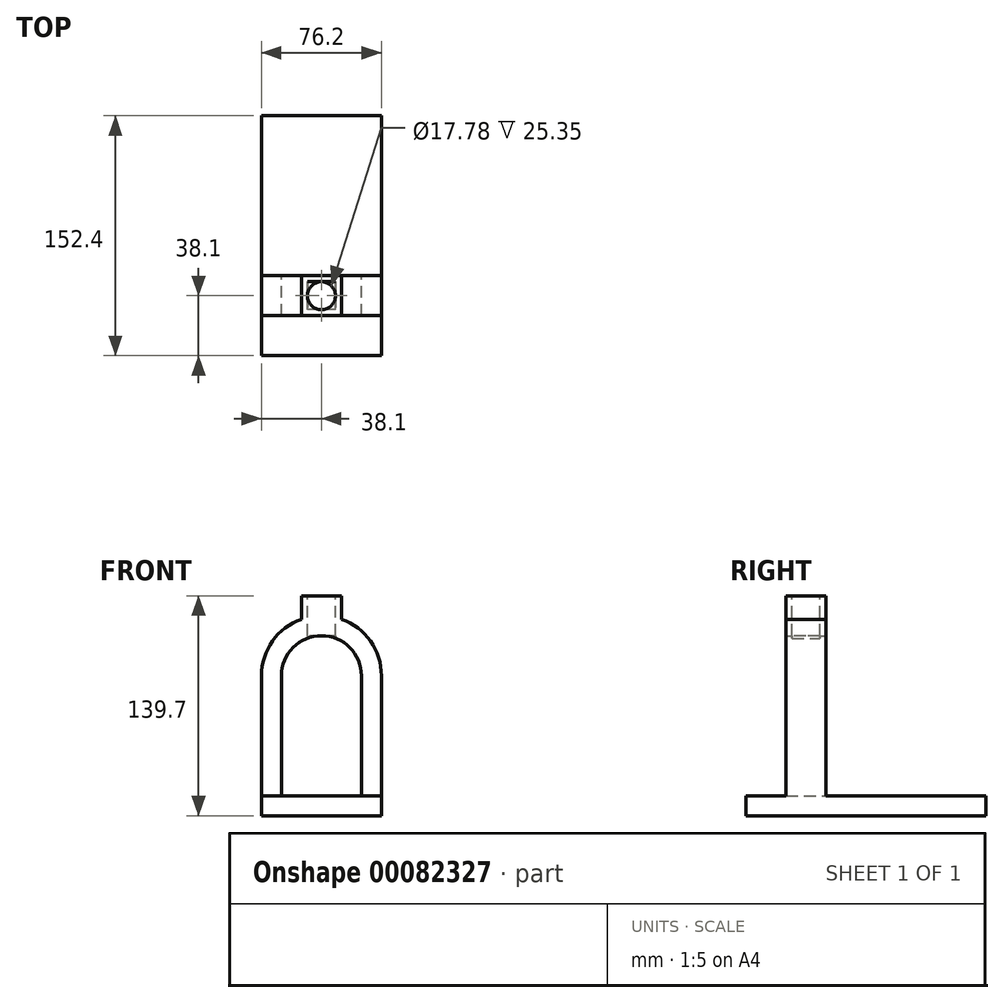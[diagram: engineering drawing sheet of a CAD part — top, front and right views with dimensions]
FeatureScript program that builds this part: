
annotation { "Feature Type Name" : "Feature", "Feature Type Description" : "" }
export const myFeature = defineFeature(function(context is Context, id is Id, definition is map)
    precondition{}
    {
        {
            var Q0;
            Q0=qCreatedBy(makeId("Front.planeOp"),FACE);
            var sketch = newSketch(context, id + "F0", { "sketchPlane" : qUnion([Q0])});
            skArc(sketch, "E0", {"start": v(25.4, 72.85) * mm, "mid": v(0, 98.25) * mm, "end": v(-25.4, 72.85) * mm});
            skArc(sketch, "E1", {"start": v(38.1, 72.85) * mm, "mid": v(31.1, 94.84) * mm, "end": v(12.7, 108.77) * mm});
            skLineSegment(sketch, "E2", {"start": v(38.1, 72.85) * mm, "end": v(38.1, -3.35) * mm});
            skLineSegment(sketch, "E3", {"start": v(-38.1, 72.85) * mm, "end": v(-38.1, -3.35) * mm});
            skLineSegment(sketch, "E4", {"start": v(-25.4, 72.85) * mm, "end": v(-25.4, -3.35) * mm});
            skLineSegment(sketch, "E5", {"start": v(25.4, 72.85) * mm, "end": v(25.4, -3.35) * mm});
            skLineSegment(sketch, "E6", {"start": v(38.1, -3.35) * mm, "end": v(25.4, -3.35) * mm});
            skLineSegment(sketch, "E7.trimOffspring", {"start": v(-25.4, -3.35) * mm, "end": v(-38.1, -3.35) * mm});
            skLineSegment(sketch, "E8", {"start": v(0, 123.65) * mm, "end": v(12.7, 123.65) * mm});
            skLineSegment(sketch, "E9", {"start": v(0, 123.65) * mm, "end": v(-12.7, 123.65) * mm});
            skLineSegment(sketch, "E10", {"start": v(-12.7, 123.65) * mm, "end": v(-12.7, 108.77) * mm});
            skLineSegment(sketch, "E11", {"start": v(12.7, 123.65) * mm, "end": v(12.7, 108.77) * mm});
            skArc(sketch, "E12.trimOffspring", {"start": v(-12.7, 108.77) * mm, "mid": v(-31.1, 94.84) * mm, "end": v(-38.1, 72.85) * mm});
            skSolve(sketch);
        }
        {
            var Q0;
            Q0 = qSketchRegion(id + "F0", true);
            extrude(context, id + "F1", {"entities" : qUnion([Q0]), "depth" : 25.4 * mm});
        }
        {
            var Q0;
            Q0=makeQuery(id+"F1.opExtrude","SWEPT_FACE",FACE,{"disambiguationData":[OSD([sQuery(id+"F0.wireOp",EDGE,"E8"),sQuery(id+"F0.wireOp",EDGE,"E9")])]});
            var sketch = newSketch(context, id + "F2", { "sketchPlane" : qUnion([Q0])});
            skCircle(sketch, "E13", {"center": v(0, -12.7) * mm, "radius": 8.9 * mm});
            skSolve(sketch);
        }
        {
            var Q0;
            Q0 = qSketchRegion(id + "F2", true);
            extrude(context, id + "F3", {"entities" : qUnion([Q0]), "operationType" : NewBodyOperationType.REMOVE, "oppositeDirection" : true, "depth" : 97.98 * mm});
        }
        {
            var Q0;
            Q0=qCreatedBy(makeId("Top.planeOp"),FACE);
            var sketch = newSketch(context, id + "F4", { "sketchPlane" : qUnion([Q0])});
            skCircle(sketch, "E14", {"center": v(0, -12.7) * mm, "radius": 8.9 * mm});
            skLineSegment(sketch, "E15.bottom", {"start": v(8.89, -3.8) * mm, "end": v(-8.9, -3.81) * mm});
            skLineSegment(sketch, "E15.top", {"start": v(8.9, -21.6) * mm, "end": v(-8.89, -21.6) * mm});
            skLineSegment(sketch, "E15.left", {"start": v(8.89, -3.8) * mm, "end": v(8.9, -21.59) * mm});
            skLineSegment(sketch, "E15.right", {"start": v(-8.9, -3.81) * mm, "end": v(-8.89, -21.59) * mm});
            skSolve(sketch);
        }
        {
            var Q0;
            Q0 = qSketchRegion(id + "F4", true);
            extrude(context, id + "F5", {"entities" : qUnion([Q0]), "operationType" : NewBodyOperationType.REMOVE, "depth" : 98.3 * mm});
        }
        {
            var Q0;
            Q0=makeQuery(id+"F1.opExtrude","SWEPT_FACE",FACE,{"disambiguationData":[OSD([sQuery(id+"F0.wireOp",EDGE,"E7.trimOffspring")])]});
            var sketch = newSketch(context, id + "F6", { "sketchPlane" : qUnion([Q0])});
            skLineSegment(sketch, "E16.bottom", {"start": v(-38.1, 25.4) * mm, "end": v(38.1, 25.4) * mm});
            skLineSegment(sketch, "E16.top", {"start": v(-38.1, -101.6) * mm, "end": v(38.1, -101.6) * mm});
            skLineSegment(sketch, "E16.left", {"start": v(-38.1, 25.4) * mm, "end": v(-38.1, -101.6) * mm});
            skLineSegment(sketch, "E16.right", {"start": v(38.1, 25.4) * mm, "end": v(38.1, -101.6) * mm});
            skSolve(sketch);
        }
        {
            var Q0;
            Q0 = qSketchRegion(id + "F6", true);
            extrude(context, id + "F7", {"entities" : qUnion([Q0]), "operationType" : NewBodyOperationType.ADD, "depth" : 12.7 * mm});
        }
        {
            var Q0;
            Q0=makeQuery(id+"F7.boolean.opBoolean","MERGE",FACE,{"derivedFrom":[makeQuery(id+"F1.opExtrude","CAP_FACE",FACE,{"disambiguationData":[OSD([sQuery(id+"F0.wireOp",EDGE,"E0"),sQuery(id+"F0.wireOp",EDGE,"E1"),sQuery(id+"F0.wireOp",EDGE,"E2"),sQuery(id+"F0.wireOp",EDGE,"E3"),sQuery(id+"F0.wireOp",EDGE,"E4"),sQuery(id+"F0.wireOp",EDGE,"E5"),sQuery(id+"F0.wireOp",EDGE,"E6"),sQuery(id+"F0.wireOp",EDGE,"E7.trimOffspring"),sQuery(id+"F0.wireOp",EDGE,"E8"),sQuery(id+"F0.wireOp",EDGE,"E9"),sQuery(id+"F0.wireOp",EDGE,"E10"),sQuery(id+"F0.wireOp",EDGE,"E11"),sQuery(id+"F0.wireOp",EDGE,"E12.trimOffspring")])],"isStart":false}),makeQuery(id+"F7.opExtrude","SWEPT_FACE",FACE,{"disambiguationData":[OSD([sQuery(id+"F6.wireOp",EDGE,"E16.bottom")])]})]});
            var sketch = newSketch(context, id + "F8", { "sketchPlane" : qUnion([Q0])});
            skLineSegment(sketch, "E17.bottom", {"start": v(38.1, -16.05) * mm, "end": v(0, -16.05) * mm});
            skLineSegment(sketch, "E17.top", {"start": v(38.1, -3.35) * mm, "end": v(0, -3.35) * mm});
            skLineSegment(sketch, "E17.left", {"start": v(38.1, -16.05) * mm, "end": v(38.1, -3.35) * mm});
            skLineSegment(sketch, "E18.bottom", {"start": v(-38.1, -16.05) * mm, "end": v(0, -16.05) * mm});
            skLineSegment(sketch, "E18.top", {"start": v(-38.1, -3.35) * mm, "end": v(0, -3.35) * mm});
            skLineSegment(sketch, "E18.left", {"start": v(-38.1, -16.05) * mm, "end": v(-38.1, -3.35) * mm});
            skSolve(sketch);
        }
        {
            var Q0;
            Q0 = qSketchRegion(id + "F8", true);
            extrude(context, id + "F9", {"entities" : qUnion([Q0]), "operationType" : NewBodyOperationType.ADD, "depth" : 25.4 * mm});
        }
    });
